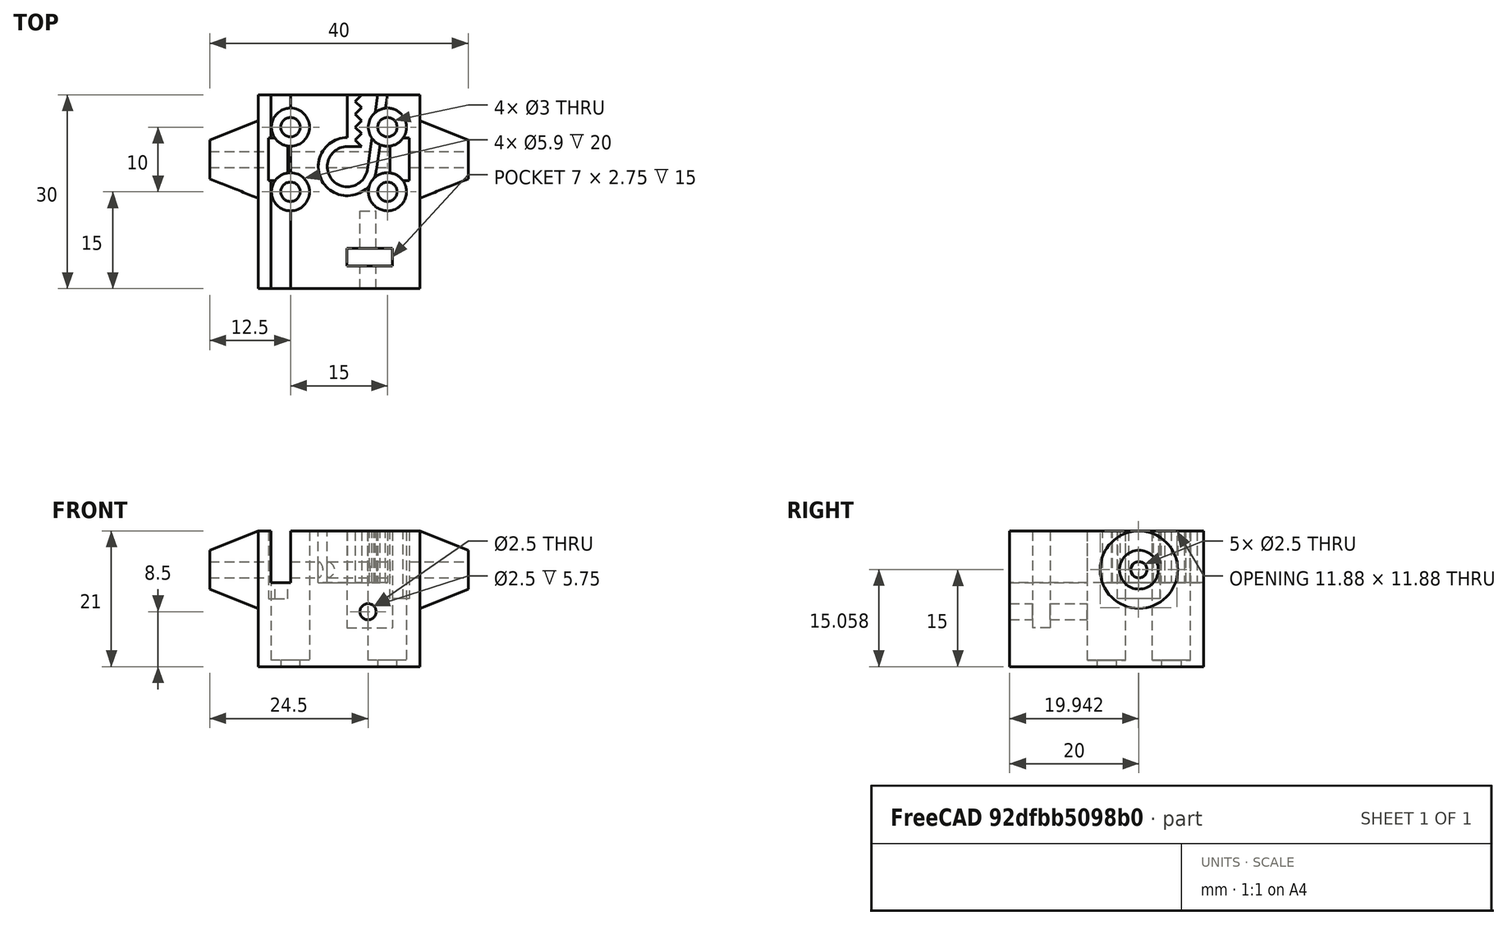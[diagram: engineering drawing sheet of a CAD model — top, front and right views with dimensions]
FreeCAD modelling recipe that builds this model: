
FCSTD DOCUMENT  (FreeCAD 2022.430R26244 +4758 (Git))
Label: as3carriage_MGN9C
License: All rights reserved
LicenseURL: http://en.wikipedia.org/wiki/All_rights_reserved
objects: Part::FeaturePython×7, App::FeaturePython×2, Part::Feature×1
note: 7 computed .brp shape members not serialized (recipe doc carries the construction recipe); baked Part::Feature solids carry a one-line shape summary decoded from their .brp

FEATURE [Part::Feature] Solid  label="carriage_MGN9C"
  TreeRank = 0
  shape: bbox 40 x 30 x 21 mm, 75 faces (baked)
FEATURE [App::FeaturePython] Constraints  # WARN: FeaturePython — macro-defined, semantics opaque (R4)
  TreeRank = 0
  _LinkVersion = 1
  _Version = 1
FEATURE [Part::FeaturePython] Parts  # WARN: FeaturePython — macro-defined, semantics opaque (R4)
  Group = -> [Solid]
  GroupMode = 0
  TreeRank = 0
  _LinkVersion = 1
FEATURE [Part::FeaturePython] Assembly  label="As3carriage_MGN9C"  # WARN: FeaturePython — macro-defined, semantics opaque (R4)
  AutoRelax = true
  BuildShape = 0
  Freeze = false
  Group = -> [Constraints,Elements,Parts]
  TreeRank = 0
  Verbose = false
  _LinkVersion = 1
  _SolverType = 1
  _Version = 1
FEATURE [App::FeaturePython] Elements  # WARN: FeaturePython — macro-defined, semantics opaque (R4)
  Group = -> [Element,Element003,Element004,Element005,Element006]
  TreeRank = 0
  _LinkVersion = 1
FEATURE [Part::FeaturePython] Element  label="Fix1"  # link proxy (typed FeaturePython)
  Detach = false
  LinkTransform = true
  LinkedObject = -> Solid [Edge20]
  TreeRank = 0
  _LinkVersion = 1
  _Parent = -> Elements
FEATURE [Part::FeaturePython] Element003  label="Fix2"  # link proxy (typed FeaturePython)
  Detach = false
  LinkTransform = true
  LinkedObject = -> Solid [Edge21]
  TreeRank = 0
  _LinkVersion = 1
  _Parent = -> Elements
FEATURE [Part::FeaturePython] Element004  label="Rot1"  # link proxy (typed FeaturePython)
  Detach = false
  LinkTransform = true
  LinkedObject = -> Solid [Edge200]
  TreeRank = 0
  _LinkVersion = 1
  _Parent = -> Elements
FEATURE [Part::FeaturePython] Element005  label="Rot2"  # link proxy (typed FeaturePython)
  Detach = false
  LinkTransform = true
  LinkedObject = -> Solid [Edge213]
  TreeRank = 0
  _LinkVersion = 1
  _Parent = -> Elements
FEATURE [Part::FeaturePython] Element006  # link proxy (typed FeaturePython)
  Detach = false
  LinkTransform = true
  LinkedObject = -> Solid [Face17]
  TreeRank = 0
  _LinkVersion = 1
  _Parent = -> Elements
